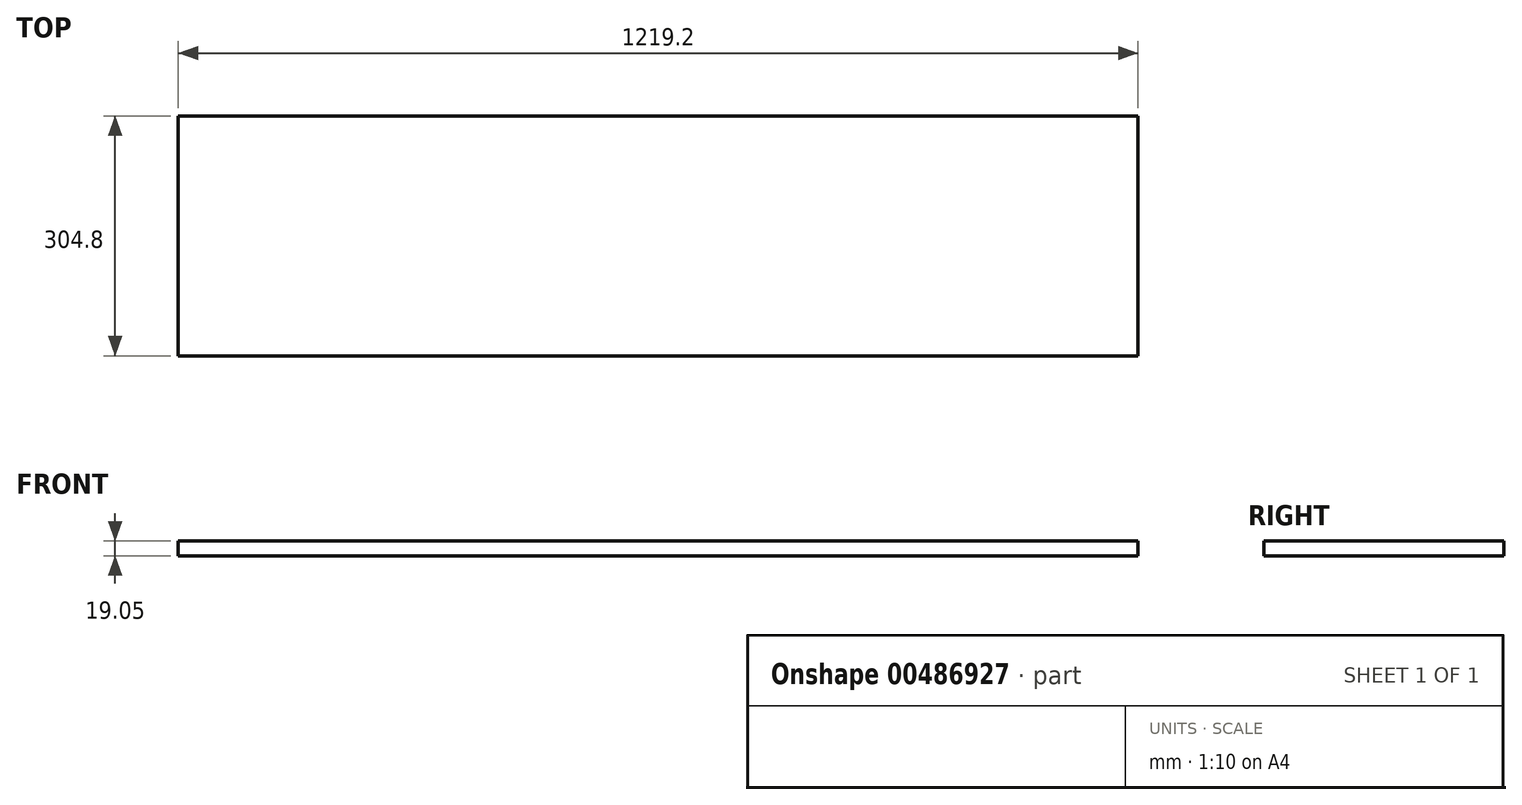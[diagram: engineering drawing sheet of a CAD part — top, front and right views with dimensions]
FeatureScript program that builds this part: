
annotation { "Feature Type Name" : "Feature", "Feature Type Description" : "" }
export const myFeature = defineFeature(function(context is Context, id is Id, definition is map)
    precondition{}
    {
        {
            var Q0;
            Q0=qCreatedBy(makeId("Top.planeOp"),FACE);
            var sketch = newSketch(context, id + "F0", { "sketchPlane" : qUnion([Q0])});
            skLineSegment(sketch, "E0.bottom", {"start": v(-594.14, -151.78) * mm, "end": v(625.06, -151.78) * mm});
            skLineSegment(sketch, "E0.top", {"start": v(-594.14, 153.02) * mm, "end": v(625.06, 153.02) * mm});
            skLineSegment(sketch, "E0.left", {"start": v(-594.14, -151.78) * mm, "end": v(-594.14, 153.02) * mm});
            skLineSegment(sketch, "E0.right", {"start": v(625.06, -151.78) * mm, "end": v(625.06, 153.02) * mm});
            skSolve(sketch);
        }
        {
            var Q0;
            Q0=makeQuery(id+"F0.imprint","IMPRINT",FACE,{"disambiguationData":[TD([[makeQuery(id+"F0.imprint","IMPRINT",EDGE,{"derivedFrom":sQuery(id+"F0.wireOp",EDGE,"E0.bottom")}),1.0]])]});
            extrude(context, id + "F1", {"entities" : qUnion([Q0]), "oppositeDirection" : true, "depth" : 19.05 * mm});
        }
    });
